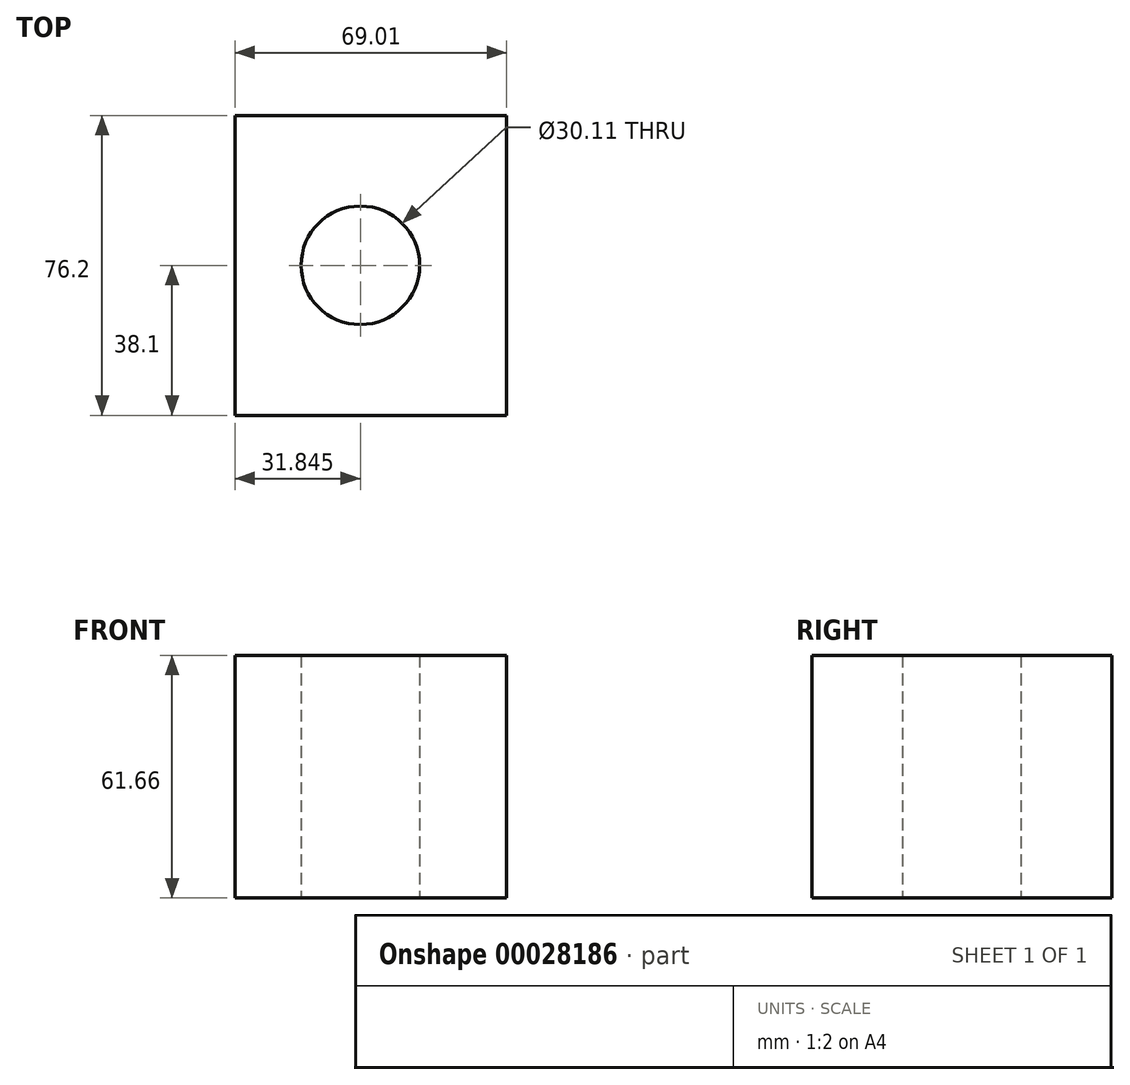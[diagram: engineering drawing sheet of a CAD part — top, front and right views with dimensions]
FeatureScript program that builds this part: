
annotation { "Feature Type Name" : "Feature", "Feature Type Description" : "" }
export const myFeature = defineFeature(function(context is Context, id is Id, definition is map)
    precondition{}
    {
        {
            var Q0;
            Q0=qCreatedBy(makeId("Top.planeOp"),FACE);
            var sketch = newSketch(context, id + "F0", { "sketchPlane" : qUnion([Q0])});
            skLineSegment(sketch, "E0.bottom", {"start": v(-25.53, -38.1) * mm, "end": v(43.48, -38.1) * mm});
            skLineSegment(sketch, "E0.top", {"start": v(-25.53, 38.1) * mm, "end": v(43.48, 38.1) * mm});
            skLineSegment(sketch, "E0.left", {"start": v(-25.53, -38.1) * mm, "end": v(-25.53, 38.1) * mm});
            skLineSegment(sketch, "E0.right", {"start": v(43.48, -38.1) * mm, "end": v(43.48, 38.1) * mm});
            skCircle(sketch, "E1", {"center": v(6.31, 0) * mm, "radius": 15.05 * mm});
            skSolve(sketch);
        }
        {
            var Q0;
            Q0=makeQuery(id+"F0.imprint","IMPRINT",FACE,{"disambiguationData":[TD([[makeQuery(id+"F0.imprint","IMPRINT",EDGE,{"derivedFrom":sQuery(id+"F0.wireOp",EDGE,"E0.bottom")}),1.0]])]});
            extrude(context, id + "F1", {"entities" : qUnion([Q0]), "depth" : 61.66 * mm});
        }
    });
